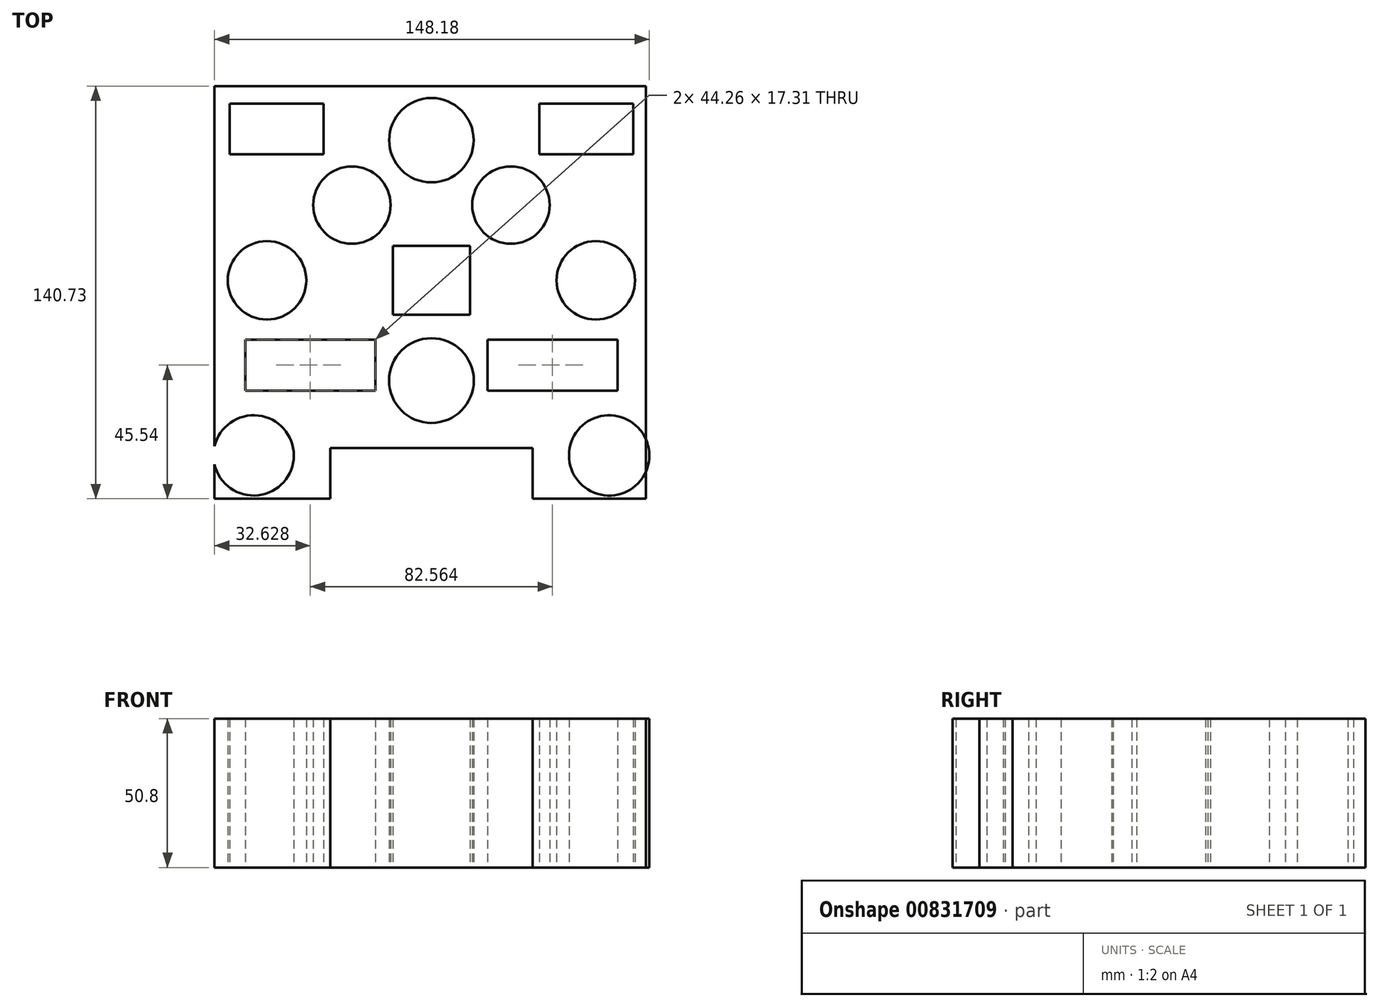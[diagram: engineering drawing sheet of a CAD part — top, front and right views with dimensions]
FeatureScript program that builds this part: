
annotation { "Feature Type Name" : "Feature", "Feature Type Description" : "" }
export const myFeature = defineFeature(function(context is Context, id is Id, definition is map)
    precondition{}
    {
        {
            var Q0;
            Q0=qCreatedBy(makeId("Top.planeOp"),FACE);
            var sketch = newSketch(context, id + "F0", { "sketchPlane" : qUnion([Q0])});
            skLineSegment(sketch, "E0.bottom", {"start": v(-73.9, 66.25) * mm, "end": v(73.06, 66.25) * mm});
            skLineSegment(sketch, "E0.top", {"start": v(-73.9, -74.48) * mm, "end": v(73.06, -74.48) * mm});
            skLineSegment(sketch, "E0.left", {"start": v(-73.9, 66.25) * mm, "end": v(-73.9, -74.48) * mm});
            skLineSegment(sketch, "E0.right", {"start": v(73.06, 66.25) * mm, "end": v(73.06, -74.48) * mm});
            skLineSegment(sketch, "E1.bottom", {"start": v(-68.8, 60.3) * mm, "end": v(-36.74, 60.3) * mm});
            skLineSegment(sketch, "E1.top", {"start": v(-68.8, 42.98) * mm, "end": v(-36.74, 42.98) * mm});
            skLineSegment(sketch, "E1.left", {"start": v(-68.8, 60.3) * mm, "end": v(-68.8, 42.98) * mm});
            skLineSegment(sketch, "E1.right", {"start": v(-36.74, 60.3) * mm, "end": v(-36.74, 42.98) * mm});
            skCircle(sketch, "E2", {"center": v(-27.1, 25.68) * mm, "radius": 13.19 * mm});
            skLineSegment(sketch, "E3", {"start": v(0, 11.77) * mm, "end": v(-13.2, 11.77) * mm});
            skLineSegment(sketch, "E4", {"start": v(-13.2, 11.77) * mm, "end": v(-13.2, 0) * mm});
            skLineSegment(sketch, "E5.MirrorCS", {"start": v(0, 11.77) * mm, "end": v(13.2, 11.77) * mm});
            skLineSegment(sketch, "E6.MirrorCS", {"start": v(13.2, 11.77) * mm, "end": v(13.2, 0) * mm});
            skCircle(sketch, "E7.MirrorC", {"center": v(27.1, 25.68) * mm, "radius": 13.19 * mm});
            skLineSegment(sketch, "E8.MirrorCS", {"start": v(36.74, 60.3) * mm, "end": v(36.74, 42.98) * mm});
            skLineSegment(sketch, "E9.MirrorCS", {"start": v(68.8, 60.3) * mm, "end": v(36.74, 60.3) * mm});
            skLineSegment(sketch, "E10.MirrorCS", {"start": v(68.8, 60.3) * mm, "end": v(68.8, 42.98) * mm});
            skLineSegment(sketch, "E11.MirrorCS", {"start": v(68.8, 42.98) * mm, "end": v(36.74, 42.98) * mm});
            skLineSegment(sketch, "E12.MirrorCS", {"start": v(-13.2, -11.77) * mm, "end": v(-13.2, 0) * mm});
            skLineSegment(sketch, "E13.MirrorCS", {"start": v(13.2, -11.77) * mm, "end": v(13.2, 0) * mm});
            skLineSegment(sketch, "E14.MirrorCS", {"start": v(0, -11.77) * mm, "end": v(-13.2, -11.77) * mm});
            skCircle(sketch, "E15", {"center": v(-60.57, -59.72) * mm, "radius": 13.7 * mm});
            skCircle(sketch, "E16.MirrorC", {"center": v(60.57, -59.72) * mm, "radius": 13.7 * mm});
            skLineSegment(sketch, "E17.MirrorCS", {"start": v(0, -11.77) * mm, "end": v(13.2, -11.77) * mm});
            skLineSegment(sketch, "E18", {"start": v(0, -57.17) * mm, "end": v(-34.47, -57.17) * mm});
            skLineSegment(sketch, "E19", {"start": v(-34.47, -57.17) * mm, "end": v(-34.47, -74.48) * mm});
            skLineSegment(sketch, "E20.MirrorCS", {"start": v(0, -57.17) * mm, "end": v(34.47, -57.17) * mm});
            skLineSegment(sketch, "E21.MirrorCS", {"start": v(34.47, -57.17) * mm, "end": v(34.47, -74.48) * mm});
            skLineSegment(sketch, "E22.bottom", {"start": v(19.15, -20.29) * mm, "end": v(63.41, -20.29) * mm});
            skLineSegment(sketch, "E22.top", {"start": v(19.15, -37.6) * mm, "end": v(63.41, -37.6) * mm});
            skLineSegment(sketch, "E22.left", {"start": v(19.15, -20.29) * mm, "end": v(19.15, -37.6) * mm});
            skLineSegment(sketch, "E22.right", {"start": v(63.41, -20.29) * mm, "end": v(63.41, -37.6) * mm});
            skLineSegment(sketch, "E23.MirrorCS", {"start": v(-19.15, -20.29) * mm, "end": v(-19.15, -37.6) * mm});
            skLineSegment(sketch, "E24.MirrorCS", {"start": v(-19.15, -37.6) * mm, "end": v(-63.41, -37.6) * mm});
            skLineSegment(sketch, "E25.MirrorCS", {"start": v(-63.41, -20.29) * mm, "end": v(-63.41, -37.6) * mm});
            skLineSegment(sketch, "E26.MirrorCS", {"start": v(-19.15, -20.29) * mm, "end": v(-63.41, -20.29) * mm});
            skCircle(sketch, "E27", {"center": v(-56.04, 0) * mm, "radius": 13.37 * mm});
            skCircle(sketch, "E28.MirrorC", {"center": v(56.04, 0) * mm, "radius": 13.37 * mm});
            skCircle(sketch, "E29", {"center": v(0, 47.8) * mm, "radius": 14.39 * mm});
            skCircle(sketch, "E30", {"center": v(0, -34.19) * mm, "radius": 14.45 * mm});
            skSolve(sketch);
        }
        {
            var Q0;
            {var subQ0=sQuery(id+"F0.wireOp",EDGE,"E15");var subQ1=sQuery(id+"F0.wireOp",EDGE,"E0.left");var subQ2=makeQuery(id+"F0.imprint","INTERSECT",VERTEX,{"disambiguationData":[OD(0.0)],"derivedFrom":[subQ1,subQ0]});Q0=makeQuery(id+"F0.imprint","IMPRINT",FACE,{"disambiguationData":[TD([[makeQuery(id+"F0.imprint","IMPRINT",EDGE,{"disambiguationData":[TD([[subQ2,-1.0]])],"derivedFrom":subQ1}),-1.0]])]});}
            var Q1;
            {var subQ0=sQuery(id+"F0.wireOp",EDGE,"E16.MirrorC");var subQ1=sQuery(id+"F0.wireOp",EDGE,"E0.right");var subQ2=makeQuery(id+"F0.imprint","INTERSECT",VERTEX,{"disambiguationData":[OD(0.0)],"derivedFrom":[subQ1,subQ0]});Q1=makeQuery(id+"F0.imprint","IMPRINT",FACE,{"disambiguationData":[TD([[makeQuery(id+"F0.imprint","IMPRINT",EDGE,{"disambiguationData":[TD([[subQ2,-1.0]])],"derivedFrom":subQ1}),1.0]])]});}
            var Q2;
            {var subQ1=sQuery(id+"F0.wireOp",EDGE,"E0.bottom");Q2=makeQuery(id+"F0.imprint","IMPRINT",FACE,{"disambiguationData":[TD([[makeQuery(id+"F0.imprint","IMPRINT",EDGE,{"derivedFrom":subQ1}),-1.0]])]});}
            extrude(context, id + "F1", {"entities" : qUnion([Q0, Q1, Q2]), "depth" : 50.8 * mm, "offsetDistance" : 25.4 * mm});
        }
    });
